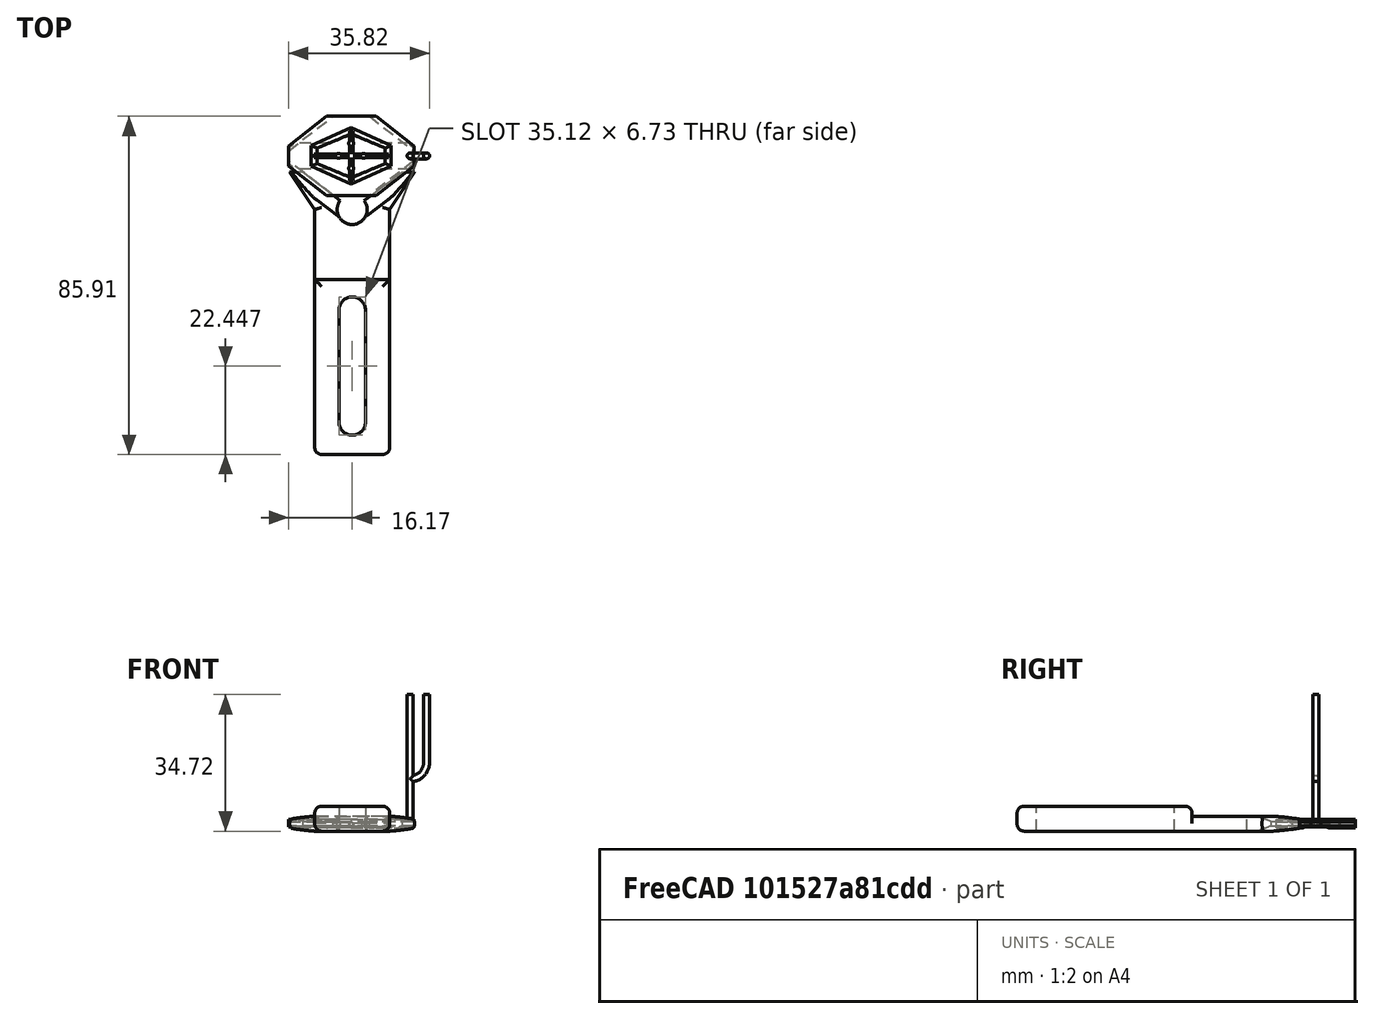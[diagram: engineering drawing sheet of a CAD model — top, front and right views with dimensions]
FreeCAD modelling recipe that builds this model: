
FCSTD DOCUMENT  (FreeCAD 0.18R16110 (Git))
Label: Headfixing clamp for Head Plate 3.5 hypoglossal1
License: All rights reserved
LicenseURL: http://en.wikipedia.org/wiki/All_rights_reserved
objects: Sketcher::SketchObject×7, Part::Feature×2, PartDesign::Pocket×2, PartDesign::SubtractivePipe×2, PartDesign::Mirrored×2, Mesh::Feature×1, PartDesign::Pad×1, PartDesign::Fillet×1, PartDesign::Body×1
note: 23 computed .brp shape members not serialized (recipe doc carries the construction recipe); baked Part::Feature solids carry a one-line shape summary decoded from their .brp

FEATURE [Sketcher::SketchObject] Sketch001  label="Cutouts"
  MapMode = 5
  Placement = pos=(-1e-15,0,6.35) rot=(0,0,-1;1.5708rad)
  expr: Constraints[6] = 0.265" / 2
  expr: Constraints[7] = 1.3825" - 2 * 0.1325"
  expr: Constraints[8] = 0.875" + 0.1325"
  sketch-geometry (10):
    g0: ArcOfCircle CenterX=25.5905 CenterY=0 CenterZ=0 NormalX=0 NormalY=0 NormalZ=1 AngleXU=0 Radius=3.3655 StartAngle=1.5708 EndAngle=4.71239
    g1: ArcOfCircle CenterX=53.975 CenterY=0 CenterZ=0 NormalX=0 NormalY=0 NormalZ=1 AngleXU=0 Radius=3.3655 StartAngle=4.71239 EndAngle=7.85398
    g2: LineSegment StartX=25.5905 StartY=-3.3655 StartZ=0 EndX=53.975 EndY=-3.3655 EndZ=0
    g3: LineSegment StartX=25.5905 StartY=3.3655 StartZ=0 EndX=53.975 EndY=3.3655 EndZ=0
    g4: LineSegment [constr] StartX=-9.525 StartY=12.6401 StartZ=0 EndX=0 EndY=0 EndZ=0
    g5: LineSegment [constr] StartX=0 StartY=0 StartZ=0 EndX=-9.525 EndY=-12.6401 EndZ=0
    g6: ArcOfCircle CenterX=0 CenterY=0 CenterZ=0 NormalX=0 NormalY=0 NormalZ=1 AngleXU=0 Radius=3.81 StartAngle=4.06662 EndAngle=8.49975
    g7: LineSegment StartX=-2.29292 StartY=-3.0428 StartZ=0 EndX=-9.525 EndY=-12.6401 EndZ=0
    g8: LineSegment StartX=-9.525 StartY=-12.6401 StartZ=0 EndX=-9.525 EndY=12.6401 EndZ=0
    g9: LineSegment StartX=-9.525 StartY=12.6401 StartZ=0 EndX=-2.29292 EndY=3.0428 EndZ=0
  constraints (25):
    c: Tangent(g0,g3) = 1.5708
    c: Tangent(g0,g2) = -1.5708
    c: Tangent(g2,g1) = -1.5708
    c: Tangent(g3,g1) = 1.5708
    c: Horizontal(g2)
    c: Equal(g0,g1)
    c: Radius(g0) = 3.3655
    c: DistanceX(g0,g1) = 28.3845
    c: DistanceX(g0) = 25.5905
    c: DistanceY(g0) = 0
    c: Symmetric(g4,g5,g-1)
    c: Coincident(g4,g5)
    c: Coincident(g4,g6)
    c: Coincident(g4,g-1)
    c: Radius(g6) = 3.81
    c: Symmetric(g6,g6,g-1)
    c: Coincident(g7,g8)
    c: Coincident(g8,g9)
    c: Coincident(g6,g9)
    c: Coincident(g6,g7)
    c: Coincident(g5,g7)
    c: Coincident(g4,g8)
    c: Parallel(g9,g4)
    c: Angle(g9,g7) = 1.85005
    c: DistanceX(g7) = -9.525
FEATURE [Mesh::Feature] wide_post_clamp_with_slot_rescaled  label="wide post clamp with slot rescaled"
FEATURE [Part::Feature] wide_post_clamp_with_slot_rescaled001
  shape: bbox 19.05 x 68.58 x 6.35 mm, 1280 faces, 0 solids (baked)
FEATURE [Part::Feature] Body002  label="Head Plate 3.5 hypoglossal1"
  Placement = pos=(-0.254,13.6398,0.8128) rot=(0,0,1;1.5708rad)
  shape: bbox 36.23 x 20.08 x 33.91 mm, 80 faces (baked)
FEATURE [Sketcher::SketchObject] Sketch006  label="Main body"
  sketch-geometry (6):
    g0: LineSegment StartX=-9.525 StartY=-62.23 StartZ=0 EndX=9.525 EndY=-62.23 EndZ=0
    g1: LineSegment StartX=9.525 StartY=-62.23 StartZ=0 EndX=9.525 EndY=0 EndZ=0
    g2: LineSegment StartX=9.525 StartY=0 StartZ=0 EndX=15.875 EndY=9.525 EndZ=0
    g3: LineSegment StartX=15.875 StartY=9.525 StartZ=0 EndX=-15.875 EndY=9.525 EndZ=0
    g4: LineSegment StartX=-15.875 StartY=9.525 StartZ=0 EndX=-9.525 EndY=0 EndZ=0
    g5: LineSegment StartX=-9.525 StartY=0 StartZ=0 EndX=-9.525 EndY=-62.23 EndZ=0
  constraints (15):
    c: Coincident(g0,g1)
    c: Coincident(g1,g2)
    c: Coincident(g2,g3)
    c: Symmetric(g0,g0,g-2)
    c: Coincident(g4,g5)
    c: Coincident(g0,g5)
    c: Coincident(g3,g4)
    c: Symmetric(g4,g1,g-2)
    c: Symmetric(g3,g2,g-2)
    c: Vertical(g5)
    c: DistanceY(g0) = -62.23
    c: DistanceY(g3) = 9.525
    c: DistanceY(g4) = 0
    c: DistanceX(g0,g0) = 19.05
    c: DistanceX(g3,g3) = 31.75
FEATURE [PartDesign::Pad] Pad
  Length = 6.35
  Length2 = 99.9998
  Profile = -> Sketch006
  Type = 0
FEATURE [PartDesign::Pocket] Pocket
  BaseFeature = -> Pad
  Length = 5.00126
  Length2 = 99.9998
  Profile = -> Sketch001
  Type = 1
FEATURE [Sketcher::SketchObject] Sketch  label="Side cut"
  MapMode = 5
  Placement = pos=(0,0,0) rot=(0.57735,0.57735,0.57735;2.0944rad)
  Support = -> [YZ_Plane]
  sketch-geometry (8):
    g0: LineSegment [constr] StartX=-62.23 StartY=6.35 StartZ=0 EndX=-17.78 EndY=6.35 EndZ=0
    g1: LineSegment StartX=-17.78 StartY=6.35 StartZ=0 EndX=-17.78 EndY=3.81 EndZ=0
    g2: LineSegment StartX=-17.78 StartY=3.81 StartZ=0 EndX=9.525 EndY=3.81 EndZ=0
    g3: LineSegment [constr] StartX=9.525 StartY=3.81 StartZ=0 EndX=9.525 EndY=0 EndZ=0
    g4: LineSegment [constr] StartX=9.525 StartY=0 StartZ=0 EndX=-62.23 EndY=0 EndZ=0
    g5: LineSegment [constr] StartX=-62.23 StartY=0 StartZ=0 EndX=-62.23 EndY=6.35 EndZ=0
    g6: LineSegment StartX=-17.78 StartY=6.35 StartZ=0 EndX=9.525 EndY=6.35 EndZ=0
    g7: LineSegment StartX=9.525 StartY=6.35 StartZ=0 EndX=9.525 EndY=3.81 EndZ=0
  constraints (23):
    c: Coincident(g0,g1)
    c: Coincident(g1,g2)
    c: Coincident(g2,g3)
    c: Coincident(g3,g4)
    c: Coincident(g4,g5)
    c: Coincident(g0,g5)
    c: Vertical(g5)
    c: Vertical(g1)
    c: Vertical(g3)
    c: Horizontal(g0)
    c: Horizontal(g2)
    c: Horizontal(g4)
    c: DistanceY(g4) = 0
    c: Distance(g5) = 6.35
    c: DistanceX(g0) = -62.23
    c: Distance(g3) = 3.81
    c: DistanceX(g0) = -17.78
    c: DistanceX(g2) = 9.525
    c: Coincident(g6,g7)
    c: Coincident(g6,g0)
    c: Coincident(g2,g7)
    c: Vertical(g7)
    c: Horizontal(g6)
FEATURE [PartDesign::Pocket] Pocket001
  BaseFeature = -> Pocket
  Length = 5.00126
  Length2 = 99.9998
  Midplane = true
  Profile = -> Sketch
  Type = 1
FEATURE [Sketcher::SketchObject] Sketch007  label="Clamp V profile"
  MapMode = 5
  Placement = pos=(0,9.525,0) rot=(0,0.707107,0.707107;3.14159rad)
  Support = -> [Pocket001]
  expr: Constraints[10] = 42thou / 2
  expr: Constraints[9] = 26.5deg / 2
  expr: Constraints[6] = tan(106deg / 2) * 0.375"
  sketch-geometry (4):
    g0: LineSegment StartX=12.1321 StartY=5.08 StartZ=0 EndX=21.8198 EndY=4.59994 EndZ=0
    g1: LineSegment StartX=21.8198 StartY=4.59994 StartZ=0 EndX=12.6401 EndY=2.4384 EndZ=0
    g2: LineSegment [constr] StartX=0 StartY=1.905 StartZ=0 EndX=38.1 EndY=1.905 EndZ=0
    g3: LineSegment StartX=12.1321 StartY=5.08 StartZ=0 EndX=12.6401 EndY=2.4384 EndZ=0
  constraints (13):
    c: Coincident(g0,g1)
    c: DistanceY(g2) = 1.905
    c: Horizontal(g2)
    c: DistanceX(g2) = 0
    c: DistanceX(g2,g2) = 38.1
    c: DistanceX(g0,g1) = 0.508
    c: DistanceX(g1) = 12.6401
    c: Coincident(g1,g3)
    c: Coincident(g0,g3)
    c: Angle(g2,g1) = 0.231256
    c: Distance(g1,g2) = 0.5334
    c: Distance(g0,g2) = 3.175
    c: Distance(g0,g2) = 2.69494
FEATURE [Sketcher::SketchObject] Sketch008  label="Clamp V path"
  MapMode = 5
  Placement = pos=(0,0,0) rot=(0.230238,0.68811,0.68811;2.689rad)
  Support = -> [Pocket001]
  sketch-geometry (1):
    g0: LineSegment StartX=-2.794 StartY=0 StartZ=0 EndX=19.05 EndY=0 EndZ=0
  constraints (4):
    c: DistanceX(g0) = -2.794
    c: DistanceX(g0) = 19.05
    c: Horizontal(g0)
    c: DistanceY(g0) = 0
FEATURE [PartDesign::SubtractivePipe] SubtractivePipe
  AuxilleryCurvelinear = true
  AuxillerySpineTangent = false
  BaseFeature = -> Pocket001
  Binormal = (0,0,0)
  Mode = 0
  Profile = -> Sketch007
  Spine = -> Sketch008 [Edge1]
  SpineTangent = false
  Transformation = 0
  Transition = 0
FEATURE [PartDesign::Mirrored] Mirrored
  BaseFeature = -> SubtractivePipe
  MirrorPlane = -> YZ_Plane
  Originals = -> [SubtractivePipe]
FEATURE [Sketcher::SketchObject] Sketch009  label="Clamp V profile001"
  MapMode = 5
  Placement = pos=(0,9.525,0) rot=(0,0.707107,0.707107;3.14159rad)
  Support = -> [Mirrored]
  expr: Constraints[10] = 42thou / 2
  expr: Constraints[9] = 26.5deg / 2
  expr: Constraints[6] = tan(106deg / 2) * 0.375"
  sketch-geometry (7):
    g0: LineSegment [constr] StartX=12.1321 StartY=5.08 StartZ=0 EndX=21.8198 EndY=4.59994 EndZ=0
    g1: LineSegment [constr] StartX=21.8198 StartY=4.59994 StartZ=0 EndX=12.6401 EndY=2.4384 EndZ=0
    g2: LineSegment [constr] StartX=0 StartY=1.905 StartZ=0 EndX=38.1 EndY=1.905 EndZ=0
    g3: LineSegment [constr] StartX=12.1321 StartY=5.08 StartZ=0 EndX=12.6401 EndY=2.4384 EndZ=0
    g4: LineSegment StartX=12.1321 StartY=-1.27 StartZ=0 EndX=21.8198 EndY=-0.78994 EndZ=0
    g5: LineSegment StartX=21.8198 StartY=-0.78994 StartZ=0 EndX=12.6401 EndY=1.3716 EndZ=0
    g6: LineSegment StartX=12.1321 StartY=-1.27 StartZ=0 EndX=12.6401 EndY=1.3716 EndZ=0
  constraints (19):
    c: Coincident(g0,g1)
    c: DistanceY(g2) = 1.905
    c: Horizontal(g2)
    c: DistanceX(g2) = 0
    c: DistanceX(g2,g2) = 38.1
    c: DistanceX(g0,g1) = 0.508
    c: DistanceX(g1) = 12.6401
    c: Coincident(g1,g3)
    c: Coincident(g0,g3)
    c: Angle(g2,g1) = 0.231256
    c: Distance(g1,g2) = 0.5334
    c: Distance(g0,g2) = 3.175
    c: Distance(g0,g2) = 2.69494
    c: Coincident(g4,g5)
    c: Coincident(g5,g6)
    c: Coincident(g4,g6)
    c: Symmetric(g1,g5,g2)
    c: Symmetric(g0,g4,g2)
    c: Symmetric(g4,g0,g2)
FEATURE [Sketcher::SketchObject] Sketch010  label="Clamp V path001"
  MapMode = 5
  Placement = pos=(0,0,0) rot=(0.230238,0.68811,0.68811;2.689rad)
  Support = -> [Pocket001]
  sketch-geometry (1):
    g0: LineSegment StartX=-2.794 StartY=0 StartZ=0 EndX=19.05 EndY=0 EndZ=0
  constraints (4):
    c: DistanceX(g0) = -2.794
    c: DistanceX(g0) = 19.05
    c: Horizontal(g0)
    c: DistanceY(g0) = 0
FEATURE [PartDesign::SubtractivePipe] SubtractivePipe001
  AuxilleryCurvelinear = true
  AuxillerySpineTangent = false
  BaseFeature = -> Mirrored
  Binormal = (0,0,0)
  Mode = 0
  Profile = -> Sketch009
  Spine = -> Sketch010 [Edge1]
  SpineTangent = false
  Transformation = 0
  Transition = 0
FEATURE [PartDesign::Mirrored] Mirrored001
  BaseFeature = -> SubtractivePipe001
  MirrorPlane = -> Sketch009 [V_Axis]
  Originals = -> [SubtractivePipe001]
FEATURE [PartDesign::Fillet] Fillet
  Base = -> Mirrored001 [Edge38,Edge12,Edge8,Edge37,Edge14,Edge26,Edge6,Edge4,Edge5,Edge10,Edge3,Edge21,Edge20,Edge2,Edge1]
  BaseFeature = -> Mirrored001
  Radius = 1.778
FEATURE [PartDesign::Body] Body
  Group = -> [Sketch001,Sketch006,Pad,Pocket,Sketch,Pocket001,Sketch007,Sketch008,SubtractivePipe,Mirrored,Sketch009,Sketch010,SubtractivePipe001,Mirrored001,Fillet]
  Origin = -> Origin
  Tip = -> Fillet
